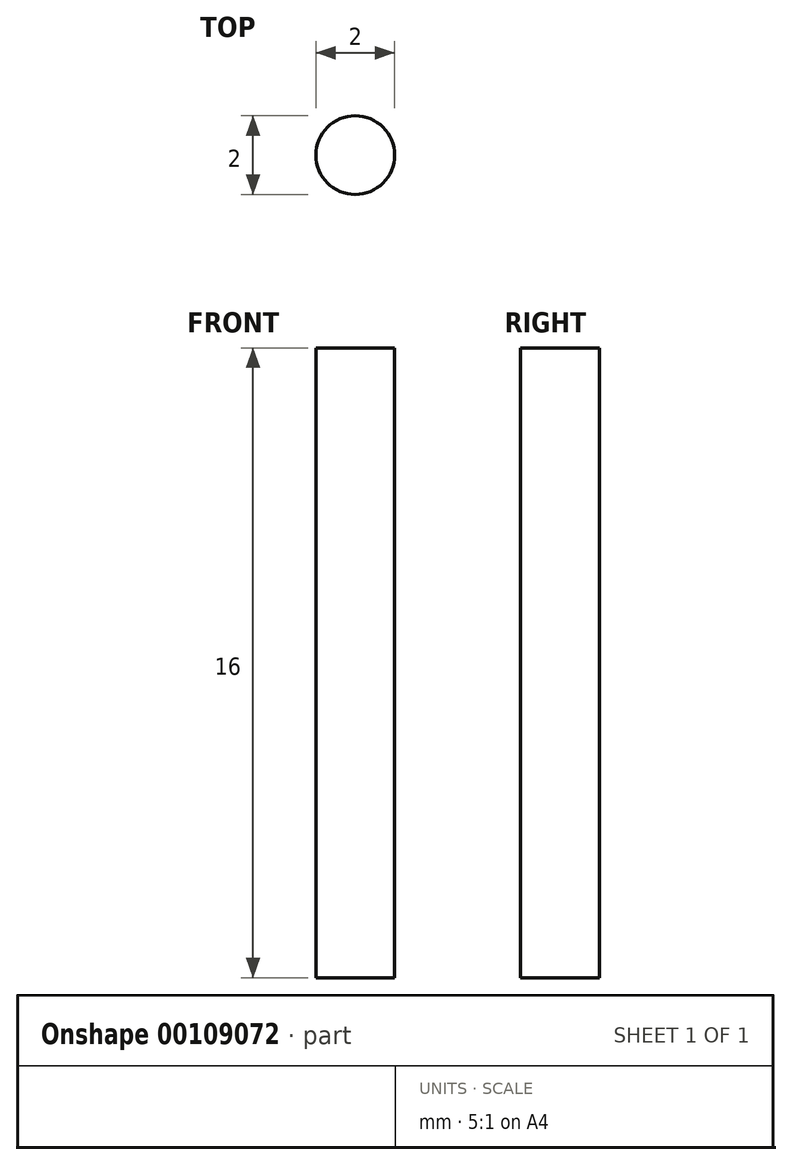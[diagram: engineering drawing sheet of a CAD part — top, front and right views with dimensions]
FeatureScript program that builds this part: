
annotation { "Feature Type Name" : "Feature", "Feature Type Description" : "" }
export const myFeature = defineFeature(function(context is Context, id is Id, definition is map)
    precondition{}
    {
        {
            var Q0;
            Q0=qCreatedBy(makeId("Top.planeOp"),FACE);
            var sketch = newSketch(context, id + "F0", { "sketchPlane" : qUnion([Q0])});
            skCircle(sketch, "E0", {"center": v(0, 0) * mm, "radius": 1 * mm});
            skSolve(sketch);
        }
        {
            var Q0;
            Q0 = qSketchRegion(id + "F0", true);
            extrude(context, id + "F1", {"entities" : qUnion([Q0]), "depth" : 16 * mm});
        }
    });
